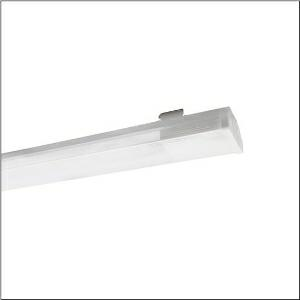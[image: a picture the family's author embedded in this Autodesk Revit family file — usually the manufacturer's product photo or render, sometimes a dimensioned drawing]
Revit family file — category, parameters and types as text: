
# Revit family: modario_31_gen_2_53bm811du4l3d2_784a
name_source: partatom
category: Lighting Fixtures
units: mm (PartAtom-declared; Revit-internal decimal feet)

## family parameters
Cut with Voids When Loaded = No
Host = Face
Light Source = No
Part Type = Normal
Room Calculation Point = No
Round Connector Dimension = Use Diameter
Shared = No

## types (1)
- --- (1 x LED, 23600 lm, 128.4 W, 4000K)
    Apparent Load = 128 VA
    CIE Flux Codes = 50 78 94 90 100
    Color Rendering = 80
    Color Temperature = 4000K
    Default Elevation = 1800 mm
    Description = Modario 31 Gen.2, luminaire insert, of sheet steel, coil coated, white, length: 2.392mm, width: 81mm, height: 82mm, 8x system unit, system units: 299mm, LED rated luminous flux: 23.600lm, light colour: 840, SDCM (Standard Deviation of Colour Matching)MacAdam ≤ 3 SDCM (initial), control gear: DALI 2, control gear: ECG DALI, with plug, 5-pole, with phase selection, mains connection: 220..240V, AC, 50/60Hz, rated input power: 128W, through-wiring accessed according to module size, primary optical cover: cover, of PMMA, light emission: direct distribution, primary light characteristic: symmetric, protection rating (complete): IP20, protection rating (LED compartment): IP50, insulation class (complete): insulation class I (protective earthing), certification: CE, ENEC, VDE, UKCA, impact resistance: IK03, permissible ambient temperature for indoor applications: -40..+35°C, corresponds to IFS (International Featured Standards) requirements for safety and quality in the food industry, reducing of maximum allowable ambient temperature of 5°C with ceiling mounting, IP40 when using the optional accessory 5TP9018, packaging unit: 1 piece
    Height = 92 mm
    Lamp = 1 x LED
    Lamp Light Flux = 23600 lm
    Lamp Power = 128.4 W
    Lamp count = 1
    Length = 2392 mm
    Luminous efficacy = 184 lm/W
    Manufacturer = Siteco
    ModVariant = No
    Model = 53BM811DU4L3D2
    Mounting Place = Ceiling
    Mounting Type = Pendant
    Number of Poles = 1
    OnlyDefault = Yes
    Power Factor = 1
    Product Name = Modario 31 Gen.2
    Product group = luminaire insert | ceiling pendant
    ProductGroupID = 901
    Protection Class = Protection class I
    Protection Degree = IP 20
    RLX_Detail_Level = 1
    RLX_Emergency_Light_Flux = 0 lm
    RLX_Emergency_Type = 0
    RLX_Emergency_Type_DB = No
    RlxData = <blob elided: 38549 chars, md5=b2afbd40>
    Socket = socket
    Standby Power = 0 W
    System Light Flux = 23600 lm
    System Power = 128 W
    Type Comments = factory setting: luminous flux: 100 % | dim-lin: 254 | 594 mA
    Type Image = l_1341883.jpg
    URL = http://relux.com
    VarID = @adj_051187
    Voltage = 0 V
    Weight = 0.00 kg
    Width = 81 mm

## geometry (parser evidence)
native form markers: Blend x4, Sweep x15
no freeform markers — native parametric forms only
